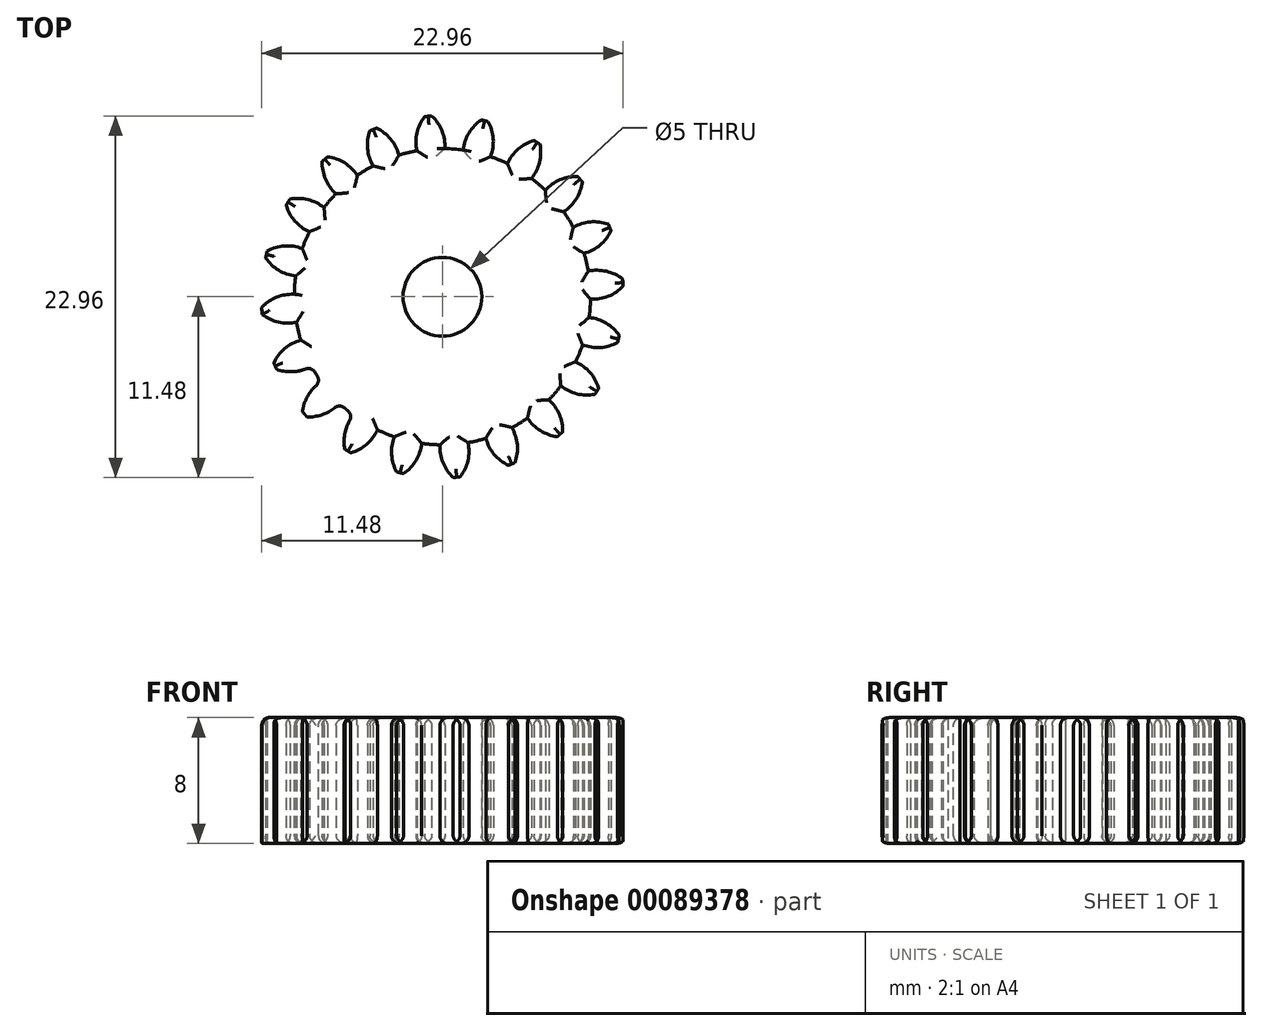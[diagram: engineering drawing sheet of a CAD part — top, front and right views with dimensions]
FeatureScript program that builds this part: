
annotation { "Feature Type Name" : "Feature", "Feature Type Description" : "" }
export const myFeature = defineFeature(function(context is Context, id is Id, definition is map)
    precondition{}
    {
        {
            assignVariable(context, id + "F0", {"name" : "GearDepth", "anyValue" : 8});
        }
        {
            assignVariable(context, id + "F1", {"name" : "TeethFillet", "anyValue" : 0.5});
        }
        {
            var Q0;
            Q0=qCreatedBy(makeId("Top.planeOp"),FACE);
            var sketch = newSketch(context, id + "F2", { "sketchPlane" : qUnion([Q0])});
            skCircle(sketch, "E0", {"center": v(0, 0) * mm, "radius": 9.4 * mm});
            skCircle(sketch, "E1", {"center": v(0, 0) * mm, "radius": 10.45 * mm, "construction": true});
            skCircle(sketch, "E2", {"center": v(0, 0) * mm, "radius": 11.5 * mm, "construction": true});
            skLineSegment(sketch, "E3", {"start": v(0, 0) * mm, "end": v(0, 17.6) * mm, "construction": true});
            skLineSegment(sketch, "E4", {"start": v(0, 0) * mm, "end": v(-1.42, 18) * mm, "construction": true});
            skLineSegment(sketch, "E5", {"start": v(0, 10.45) * mm, "end": v(-10.54, 10.45) * mm, "construction": true});
            skLineSegment(sketch, "E6", {"start": v(0, 10.45) * mm, "end": v(-10.3, 6.7) * mm, "construction": true});
            skCircle(sketch, "E7", {"center": v(0, 10.45) * mm, "radius": 2.61 * mm, "construction": true});
            skCircle(sketch, "E8", {"center": v(-2.46, 9.56) * mm, "radius": 2.61 * mm, "construction": true});
            skArc(sketch, "E9", {"start": v(-4.91, 10.45) * mm, "mid": v(-4.92, 10.42) * mm, "end": v(-4.94, 10.39) * mm});
            skArc(sketch, "E10.trimOffspring", {"start": v(0.15, 9.4) * mm, "mid": v(-0.03, 10.54) * mm, "end": v(-0.68, 11.48) * mm});
            skArc(sketch, "E11.MirrorCS", {"start": v(-1.62, 9.27) * mm, "mid": v(-1.62, 10.41) * mm, "end": v(-1.12, 11.45) * mm});
            skLineSegment(sketch, "E12", {"start": v(-1.12, 11.45) * mm, "end": v(-0.68, 11.48) * mm});
            skArc(sketch, "E13.1.0", {"start": v(-2.76, 9) * mm, "mid": v(-3.29, 10.01) * mm, "end": v(-4.2, 10.7) * mm});
            skLineSegment(sketch, "E13.1.1", {"start": v(-4.6, 10.54) * mm, "end": v(-4.2, 10.7) * mm});
            skArc(sketch, "E13.1.2", {"start": v(-4.4, 8.31) * mm, "mid": v(-4.76, 9.4) * mm, "end": v(-4.6, 10.54) * mm});
            skArc(sketch, "E13.2.0", {"start": v(-5.4, 7.7) * mm, "mid": v(-6.22, 8.5) * mm, "end": v(-7.3, 8.89) * mm});
            skLineSegment(sketch, "E13.2.1", {"start": v(-7.64, 8.6) * mm, "end": v(-7.3, 8.89) * mm});
            skArc(sketch, "E13.2.2", {"start": v(-6.76, 6.54) * mm, "mid": v(-7.43, 7.47) * mm, "end": v(-7.64, 8.6) * mm});
            skArc(sketch, "E13.3.0", {"start": v(-7.52, 5.65) * mm, "mid": v(-8.54, 6.17) * mm, "end": v(-9.69, 6.2) * mm});
            skLineSegment(sketch, "E13.3.1", {"start": v(-9.92, 5.82) * mm, "end": v(-9.69, 6.2) * mm});
            skArc(sketch, "E13.3.2", {"start": v(-8.45, 4.13) * mm, "mid": v(-9.37, 4.81) * mm, "end": v(-9.92, 5.82) * mm});
            skArc(sketch, "E13.4.0", {"start": v(-8.9, 3.05) * mm, "mid": v(-10.03, 3.23) * mm, "end": v(-11.13, 2.9) * mm});
            skLineSegment(sketch, "E13.4.1", {"start": v(-11.23, 2.47) * mm, "end": v(-11.13, 2.9) * mm});
            skArc(sketch, "E13.4.2", {"start": v(-9.32, 1.32) * mm, "mid": v(-10.4, 1.68) * mm, "end": v(-11.23, 2.47) * mm});
            skArc(sketch, "E13.5.0", {"start": v(-9.4, 0.15) * mm, "mid": v(-10.54, -0.03) * mm, "end": v(-11.48, -0.68) * mm});
            skLineSegment(sketch, "E13.5.1", {"start": v(-11.45, -1.12) * mm, "end": v(-11.48, -0.68) * mm});
            skArc(sketch, "E13.5.2", {"start": v(-9.27, -1.62) * mm, "mid": v(-10.41, -1.62) * mm, "end": v(-11.45, -1.12) * mm});
            skArc(sketch, "E13.6.0", {"start": v(-9, -2.76) * mm, "mid": v(-10.01, -3.29) * mm, "end": v(-10.7, -4.2) * mm});
            skLineSegment(sketch, "E13.6.1", {"start": v(-10.54, -4.6) * mm, "end": v(-10.7, -4.2) * mm});
            skArc(sketch, "E13.6.2", {"start": v(-8.31, -4.4) * mm, "mid": v(-9.4, -4.76) * mm, "end": v(-10.54, -4.6) * mm});
            skArc(sketch, "E13.7.0", {"start": v(-7.7, -5.4) * mm, "mid": v(-8.5, -6.22) * mm, "end": v(-8.89, -7.3) * mm});
            skLineSegment(sketch, "E13.7.1", {"start": v(-8.6, -7.64) * mm, "end": v(-8.89, -7.3) * mm});
            skArc(sketch, "E13.7.2", {"start": v(-6.54, -6.76) * mm, "mid": v(-7.47, -7.43) * mm, "end": v(-8.6, -7.64) * mm});
            skArc(sketch, "E13.8.0", {"start": v(-5.65, -7.52) * mm, "mid": v(-6.17, -8.54) * mm, "end": v(-6.2, -9.69) * mm});
            skLineSegment(sketch, "E13.8.1", {"start": v(-5.82, -9.92) * mm, "end": v(-6.2, -9.69) * mm});
            skArc(sketch, "E13.8.2", {"start": v(-4.13, -8.45) * mm, "mid": v(-4.81, -9.37) * mm, "end": v(-5.82, -9.92) * mm});
            skArc(sketch, "E13.9.0", {"start": v(-3.05, -8.9) * mm, "mid": v(-3.23, -10.03) * mm, "end": v(-2.9, -11.13) * mm});
            skLineSegment(sketch, "E13.9.1", {"start": v(-2.47, -11.23) * mm, "end": v(-2.9, -11.13) * mm});
            skArc(sketch, "E13.9.2", {"start": v(-1.32, -9.32) * mm, "mid": v(-1.68, -10.4) * mm, "end": v(-2.47, -11.23) * mm});
            skArc(sketch, "E13.10.0", {"start": v(-0.15, -9.4) * mm, "mid": v(0.03, -10.54) * mm, "end": v(0.68, -11.48) * mm});
            skLineSegment(sketch, "E13.10.1", {"start": v(1.12, -11.45) * mm, "end": v(0.68, -11.48) * mm});
            skArc(sketch, "E13.10.2", {"start": v(1.62, -9.27) * mm, "mid": v(1.62, -10.41) * mm, "end": v(1.12, -11.45) * mm});
            skArc(sketch, "E13.11.0", {"start": v(2.76, -9) * mm, "mid": v(3.29, -10.01) * mm, "end": v(4.2, -10.7) * mm});
            skLineSegment(sketch, "E13.11.1", {"start": v(4.6, -10.54) * mm, "end": v(4.2, -10.7) * mm});
            skArc(sketch, "E13.11.2", {"start": v(4.4, -8.31) * mm, "mid": v(4.76, -9.4) * mm, "end": v(4.6, -10.54) * mm});
            skArc(sketch, "E13.12.0", {"start": v(5.4, -7.7) * mm, "mid": v(6.22, -8.5) * mm, "end": v(7.3, -8.89) * mm});
            skLineSegment(sketch, "E13.12.1", {"start": v(7.64, -8.6) * mm, "end": v(7.3, -8.89) * mm});
            skArc(sketch, "E13.12.2", {"start": v(6.76, -6.54) * mm, "mid": v(7.43, -7.47) * mm, "end": v(7.64, -8.6) * mm});
            skArc(sketch, "E13.13.0", {"start": v(7.52, -5.65) * mm, "mid": v(8.54, -6.17) * mm, "end": v(9.69, -6.2) * mm});
            skLineSegment(sketch, "E13.13.1", {"start": v(9.92, -5.82) * mm, "end": v(9.69, -6.2) * mm});
            skArc(sketch, "E13.13.2", {"start": v(8.45, -4.13) * mm, "mid": v(9.37, -4.81) * mm, "end": v(9.92, -5.82) * mm});
            skArc(sketch, "E13.14.0", {"start": v(8.9, -3.05) * mm, "mid": v(10.03, -3.23) * mm, "end": v(11.13, -2.9) * mm});
            skLineSegment(sketch, "E13.14.1", {"start": v(11.23, -2.47) * mm, "end": v(11.13, -2.9) * mm});
            skArc(sketch, "E13.14.2", {"start": v(9.32, -1.32) * mm, "mid": v(10.4, -1.68) * mm, "end": v(11.23, -2.47) * mm});
            skArc(sketch, "E13.15.0", {"start": v(9.4, -0.15) * mm, "mid": v(10.54, 0.03) * mm, "end": v(11.48, 0.68) * mm});
            skLineSegment(sketch, "E13.15.1", {"start": v(11.45, 1.12) * mm, "end": v(11.48, 0.68) * mm});
            skArc(sketch, "E13.15.2", {"start": v(9.27, 1.62) * mm, "mid": v(10.41, 1.62) * mm, "end": v(11.45, 1.12) * mm});
            skArc(sketch, "E13.16.0", {"start": v(9, 2.76) * mm, "mid": v(10.01, 3.29) * mm, "end": v(10.7, 4.2) * mm});
            skLineSegment(sketch, "E13.16.1", {"start": v(10.54, 4.6) * mm, "end": v(10.7, 4.2) * mm});
            skArc(sketch, "E13.16.2", {"start": v(8.31, 4.4) * mm, "mid": v(9.4, 4.76) * mm, "end": v(10.54, 4.6) * mm});
            skArc(sketch, "E13.17.0", {"start": v(7.7, 5.4) * mm, "mid": v(8.5, 6.22) * mm, "end": v(8.89, 7.3) * mm});
            skLineSegment(sketch, "E13.17.1", {"start": v(8.6, 7.64) * mm, "end": v(8.89, 7.3) * mm});
            skArc(sketch, "E13.17.2", {"start": v(6.54, 6.76) * mm, "mid": v(7.47, 7.43) * mm, "end": v(8.6, 7.64) * mm});
            skArc(sketch, "E13.18.0", {"start": v(5.65, 7.52) * mm, "mid": v(6.17, 8.54) * mm, "end": v(6.2, 9.69) * mm});
            skLineSegment(sketch, "E13.18.1", {"start": v(5.82, 9.92) * mm, "end": v(6.2, 9.69) * mm});
            skArc(sketch, "E13.18.2", {"start": v(4.13, 8.45) * mm, "mid": v(4.81, 9.37) * mm, "end": v(5.82, 9.92) * mm});
            skArc(sketch, "E13.19.0", {"start": v(3.05, 8.9) * mm, "mid": v(3.23, 10.03) * mm, "end": v(2.9, 11.13) * mm});
            skLineSegment(sketch, "E13.19.1", {"start": v(2.47, 11.23) * mm, "end": v(2.9, 11.13) * mm});
            skArc(sketch, "E13.19.2", {"start": v(1.32, 9.32) * mm, "mid": v(1.68, 10.4) * mm, "end": v(2.47, 11.23) * mm});
            skCircle(sketch, "E14", {"center": v(0, 0) * mm, "radius": 2.5 * mm});
            skSolve(sketch);
        }
        {
            var Q0;
            {var subQ0=sQuery(id+"F2.wireOp",EDGE,"E10.trimOffspring");Q0=makeQuery(id+"F2.imprint","IMPRINT",FACE,{"disambiguationData":[TD([[makeQuery(id+"F2.imprint","IMPRINT",EDGE,{"derivedFrom":subQ0}),1.0]])]});}
            var Q1;
            {var subQ0=sQuery(id+"F2.wireOp",EDGE,"E0");var subQ1=makeQuery(id+"F2.imprint","INTERSECT",VERTEX,{"derivedFrom":[subQ0,sQuery(id+"F2.wireOp",EDGE,"E10.trimOffspring")]});Q1=makeQuery(id+"F2.imprint","IMPRINT",FACE,{"disambiguationData":[TD([[makeQuery(id+"F2.imprint","IMPRINT",EDGE,{"disambiguationData":[TD([[subQ1,-1.0]])],"derivedFrom":subQ0}),1.0]])]});}
            var Q2;
            {var subQ0=sQuery(id+"F2.wireOp",EDGE,"E13.1.0");Q2=makeQuery(id+"F2.imprint","IMPRINT",FACE,{"disambiguationData":[TD([[makeQuery(id+"F2.imprint","IMPRINT",EDGE,{"derivedFrom":subQ0}),1.0]])]});}
            var Q3;
            {var subQ0=sQuery(id+"F2.wireOp",EDGE,"E13.2.0");Q3=makeQuery(id+"F2.imprint","IMPRINT",FACE,{"disambiguationData":[TD([[makeQuery(id+"F2.imprint","IMPRINT",EDGE,{"derivedFrom":subQ0}),1.0]])]});}
            var Q4;
            {var subQ0=sQuery(id+"F2.wireOp",EDGE,"E13.3.0");Q4=makeQuery(id+"F2.imprint","IMPRINT",FACE,{"disambiguationData":[TD([[makeQuery(id+"F2.imprint","IMPRINT",EDGE,{"derivedFrom":subQ0}),1.0]])]});}
            var Q5;
            {var subQ0=sQuery(id+"F2.wireOp",EDGE,"E13.4.0");Q5=makeQuery(id+"F2.imprint","IMPRINT",FACE,{"disambiguationData":[TD([[makeQuery(id+"F2.imprint","IMPRINT",EDGE,{"derivedFrom":subQ0}),1.0]])]});}
            var Q6;
            {var subQ0=sQuery(id+"F2.wireOp",EDGE,"E13.5.0");Q6=makeQuery(id+"F2.imprint","IMPRINT",FACE,{"disambiguationData":[TD([[makeQuery(id+"F2.imprint","IMPRINT",EDGE,{"derivedFrom":subQ0}),1.0]])]});}
            var Q7;
            {var subQ0=sQuery(id+"F2.wireOp",EDGE,"E13.6.0");Q7=makeQuery(id+"F2.imprint","IMPRINT",FACE,{"disambiguationData":[TD([[makeQuery(id+"F2.imprint","IMPRINT",EDGE,{"derivedFrom":subQ0}),1.0]])]});}
            var Q8;
            {var subQ0=sQuery(id+"F2.wireOp",EDGE,"E13.7.0");Q8=makeQuery(id+"F2.imprint","IMPRINT",FACE,{"disambiguationData":[TD([[makeQuery(id+"F2.imprint","IMPRINT",EDGE,{"derivedFrom":subQ0}),1.0]])]});}
            var Q9;
            {var subQ0=sQuery(id+"F2.wireOp",EDGE,"E13.8.0");Q9=makeQuery(id+"F2.imprint","IMPRINT",FACE,{"disambiguationData":[TD([[makeQuery(id+"F2.imprint","IMPRINT",EDGE,{"derivedFrom":subQ0}),1.0]])]});}
            var Q10;
            {var subQ0=sQuery(id+"F2.wireOp",EDGE,"E13.9.0");Q10=makeQuery(id+"F2.imprint","IMPRINT",FACE,{"disambiguationData":[TD([[makeQuery(id+"F2.imprint","IMPRINT",EDGE,{"derivedFrom":subQ0}),1.0]])]});}
            var Q11;
            {var subQ0=sQuery(id+"F2.wireOp",EDGE,"E13.10.0");Q11=makeQuery(id+"F2.imprint","IMPRINT",FACE,{"disambiguationData":[TD([[makeQuery(id+"F2.imprint","IMPRINT",EDGE,{"derivedFrom":subQ0}),1.0]])]});}
            var Q12;
            {var subQ0=sQuery(id+"F2.wireOp",EDGE,"E13.11.0");Q12=makeQuery(id+"F2.imprint","IMPRINT",FACE,{"disambiguationData":[TD([[makeQuery(id+"F2.imprint","IMPRINT",EDGE,{"derivedFrom":subQ0}),1.0]])]});}
            var Q13;
            {var subQ0=sQuery(id+"F2.wireOp",EDGE,"E13.12.0");Q13=makeQuery(id+"F2.imprint","IMPRINT",FACE,{"disambiguationData":[TD([[makeQuery(id+"F2.imprint","IMPRINT",EDGE,{"derivedFrom":subQ0}),1.0]])]});}
            var Q14;
            {var subQ0=sQuery(id+"F2.wireOp",EDGE,"E13.13.0");Q14=makeQuery(id+"F2.imprint","IMPRINT",FACE,{"disambiguationData":[TD([[makeQuery(id+"F2.imprint","IMPRINT",EDGE,{"derivedFrom":subQ0}),1.0]])]});}
            var Q15;
            {var subQ0=sQuery(id+"F2.wireOp",EDGE,"E13.14.0");Q15=makeQuery(id+"F2.imprint","IMPRINT",FACE,{"disambiguationData":[TD([[makeQuery(id+"F2.imprint","IMPRINT",EDGE,{"derivedFrom":subQ0}),1.0]])]});}
            var Q16;
            {var subQ0=sQuery(id+"F2.wireOp",EDGE,"E13.15.0");Q16=makeQuery(id+"F2.imprint","IMPRINT",FACE,{"disambiguationData":[TD([[makeQuery(id+"F2.imprint","IMPRINT",EDGE,{"derivedFrom":subQ0}),1.0]])]});}
            var Q17;
            {var subQ0=sQuery(id+"F2.wireOp",EDGE,"E13.16.0");Q17=makeQuery(id+"F2.imprint","IMPRINT",FACE,{"disambiguationData":[TD([[makeQuery(id+"F2.imprint","IMPRINT",EDGE,{"derivedFrom":subQ0}),1.0]])]});}
            var Q18;
            {var subQ0=sQuery(id+"F2.wireOp",EDGE,"E13.17.0");Q18=makeQuery(id+"F2.imprint","IMPRINT",FACE,{"disambiguationData":[TD([[makeQuery(id+"F2.imprint","IMPRINT",EDGE,{"derivedFrom":subQ0}),1.0]])]});}
            var Q19;
            {var subQ0=sQuery(id+"F2.wireOp",EDGE,"E13.18.0");Q19=makeQuery(id+"F2.imprint","IMPRINT",FACE,{"disambiguationData":[TD([[makeQuery(id+"F2.imprint","IMPRINT",EDGE,{"derivedFrom":subQ0}),1.0]])]});}
            var Q20;
            {var subQ0=sQuery(id+"F2.wireOp",EDGE,"E13.19.0");Q20=makeQuery(id+"F2.imprint","IMPRINT",FACE,{"disambiguationData":[TD([[makeQuery(id+"F2.imprint","IMPRINT",EDGE,{"derivedFrom":subQ0}),1.0]])]});}
            var Q21;
            Q21=sQuery(id+"F2.wireOp",EDGE,"E0");
            var Q22;
            Q22=sQuery(id+"F2.wireOp",EDGE,"E10.trimOffspring");
            var Q23;
            Q23=sQuery(id+"F2.wireOp",EDGE,"E12");
            var Q24;
            Q24=sQuery(id+"F2.wireOp",EDGE,"E11.MirrorCS");
            extrude(context, id + "F3", {"entities" : qUnion([Q0, Q1, Q2, Q3, Q4, Q5, Q6, Q7, Q8, Q9, Q10, Q11, Q12, Q13, Q14, Q15, Q16, Q17, Q18, Q19, Q20]), "surfaceEntities" : qUnion([Q21, Q22, Q23, Q24]), "depth" : (getVariable(context, 'GearDepth')) * mm});
        }
        {
            var Q0;
            Q0=makeQuery(id+"F3.opExtrude","CAP_EDGE",EDGE,{"disambiguationData":[OSD([sQuery(id+"F2.wireOp",EDGE,"E13.5.2")])],"isStart":false});
            var Q1;
            Q1=makeQuery(id+"F3.opExtrude","CAP_EDGE",EDGE,{"disambiguationData":[OSD([sQuery(id+"F2.wireOp",EDGE,"E13.5.1")])],"isStart":false});
            var Q2;
            {var subQ0=sQuery(id+"F2.wireOp",EDGE,"E0");Q2=makeQuery(id+"F3.opExtrude","CAP_EDGE",EDGE,{"disambiguationData":[OSD([subQ0]),TDD([makeQuery(id+"F2.imprint","IMPRINT",EDGE,{"disambiguationData":[TD([[makeQuery(id+"F2.imprint","INTERSECT",VERTEX,{"derivedFrom":[subQ0,sQuery(id+"F2.wireOp",EDGE,"E13.5.2")]}),-1.0]])],"derivedFrom":subQ0})])],"isStart":false});}
            var Q3;
            Q3=makeQuery(id+"F3.opExtrude","CAP_EDGE",EDGE,{"disambiguationData":[OSD([sQuery(id+"F2.wireOp",EDGE,"E13.6.0")])],"isStart":false});
            var Q4;
            Q4=makeQuery(id+"F3.opExtrude","CAP_EDGE",EDGE,{"disambiguationData":[OSD([sQuery(id+"F2.wireOp",EDGE,"E13.6.1")])],"isStart":false});
            var Q5;
            Q5=makeQuery(id+"F3.opExtrude","CAP_EDGE",EDGE,{"disambiguationData":[OSD([sQuery(id+"F2.wireOp",EDGE,"E13.6.2")])],"isStart":false});
            var Q6;
            {var subQ0=sQuery(id+"F2.wireOp",EDGE,"E0");Q6=makeQuery(id+"F3.opExtrude","SWEPT_FACE",FACE,{"disambiguationData":[OSD([subQ0]),TDD([makeQuery(id+"F2.imprint","IMPRINT",EDGE,{"disambiguationData":[TD([[makeQuery(id+"F2.imprint","INTERSECT",VERTEX,{"derivedFrom":[subQ0,sQuery(id+"F2.wireOp",EDGE,"E13.6.2")]}),-1.0]])],"derivedFrom":subQ0})])]});}
            var Q7;
            {var subQ0=sQuery(id+"F2.wireOp",EDGE,"E0");Q7=makeQuery(id+"F3.opExtrude","CAP_EDGE",EDGE,{"disambiguationData":[OSD([subQ0]),TDD([makeQuery(id+"F2.imprint","IMPRINT",EDGE,{"disambiguationData":[TD([[makeQuery(id+"F2.imprint","INTERSECT",VERTEX,{"derivedFrom":[subQ0,sQuery(id+"F2.wireOp",EDGE,"E13.6.2")]}),-1.0]])],"derivedFrom":subQ0})])],"isStart":false});}
            var Q8;
            Q8=makeQuery(id+"F3.opExtrude","CAP_EDGE",EDGE,{"disambiguationData":[OSD([sQuery(id+"F2.wireOp",EDGE,"E13.7.2")])],"isStart":true});
            var Q9;
            {var subQ0=sQuery(id+"F2.wireOp",EDGE,"E0");Q9=makeQuery(id+"F3.opExtrude","CAP_EDGE",EDGE,{"disambiguationData":[OSD([subQ0]),TDD([makeQuery(id+"F2.imprint","IMPRINT",EDGE,{"disambiguationData":[TD([[makeQuery(id+"F2.imprint","INTERSECT",VERTEX,{"derivedFrom":[subQ0,sQuery(id+"F2.wireOp",EDGE,"E13.7.2")]}),-1.0]])],"derivedFrom":subQ0})])],"isStart":true});}
            var Q10;
            Q10=makeQuery(id+"F3.opExtrude","CAP_EDGE",EDGE,{"disambiguationData":[OSD([sQuery(id+"F2.wireOp",EDGE,"E13.7.2")])],"isStart":false});
            var Q11;
            {var subQ0=sQuery(id+"F2.wireOp",EDGE,"E0");Q11=makeQuery(id+"F3.opExtrude","CAP_EDGE",EDGE,{"disambiguationData":[OSD([subQ0]),TDD([makeQuery(id+"F2.imprint","IMPRINT",EDGE,{"disambiguationData":[TD([[makeQuery(id+"F2.imprint","INTERSECT",VERTEX,{"derivedFrom":[subQ0,sQuery(id+"F2.wireOp",EDGE,"E13.7.2")]}),-1.0]])],"derivedFrom":subQ0})])],"isStart":false});}
            var Q12;
            Q12=makeQuery(id+"F3.opExtrude","CAP_EDGE",EDGE,{"disambiguationData":[OSD([sQuery(id+"F2.wireOp",EDGE,"E13.8.0")])],"isStart":false});
            var Q13;
            {var subQ0=sQuery(id+"F2.wireOp",EDGE,"E0");Q13=makeQuery(id+"F3.opExtrude","SWEPT_FACE",FACE,{"disambiguationData":[OSD([subQ0]),TDD([makeQuery(id+"F2.imprint","IMPRINT",EDGE,{"disambiguationData":[TD([[makeQuery(id+"F2.imprint","INTERSECT",VERTEX,{"derivedFrom":[subQ0,sQuery(id+"F2.wireOp",EDGE,"E13.7.2")]}),-1.0]])],"derivedFrom":subQ0})])]});}
            var Q14;
            Q14=makeQuery(id+"F3.opExtrude","CAP_EDGE",EDGE,{"disambiguationData":[OSD([sQuery(id+"F2.wireOp",EDGE,"E13.6.0")])],"isStart":true});
            var Q15;
            Q15=makeQuery(id+"F3.opExtrude","CAP_EDGE",EDGE,{"disambiguationData":[OSD([sQuery(id+"F2.wireOp",EDGE,"E13.8.2")])],"isStart":false});
            var Q16;
            {var subQ0=sQuery(id+"F2.wireOp",EDGE,"E0");Q16=makeQuery(id+"F3.opExtrude","CAP_EDGE",EDGE,{"disambiguationData":[OSD([subQ0]),TDD([makeQuery(id+"F2.imprint","IMPRINT",EDGE,{"disambiguationData":[TD([[makeQuery(id+"F2.imprint","INTERSECT",VERTEX,{"derivedFrom":[subQ0,sQuery(id+"F2.wireOp",EDGE,"E13.8.2")]}),-1.0]])],"derivedFrom":subQ0})])],"isStart":false});}
            var Q17;
            Q17=makeQuery(id+"F3.opExtrude","CAP_EDGE",EDGE,{"disambiguationData":[OSD([sQuery(id+"F2.wireOp",EDGE,"E13.9.0")])],"isStart":false});
            var Q18;
            Q18=makeQuery(id+"F3.opExtrude","CAP_EDGE",EDGE,{"disambiguationData":[OSD([sQuery(id+"F2.wireOp",EDGE,"E13.9.2")])],"isStart":false});
            var Q19;
            {var subQ0=sQuery(id+"F2.wireOp",EDGE,"E0");Q19=makeQuery(id+"F3.opExtrude","CAP_EDGE",EDGE,{"disambiguationData":[OSD([subQ0]),TDD([makeQuery(id+"F2.imprint","IMPRINT",EDGE,{"disambiguationData":[TD([[makeQuery(id+"F2.imprint","INTERSECT",VERTEX,{"derivedFrom":[subQ0,sQuery(id+"F2.wireOp",EDGE,"E13.9.2")]}),-1.0]])],"derivedFrom":subQ0})])],"isStart":false});}
            var Q20;
            Q20=makeQuery(id+"F3.opExtrude","CAP_EDGE",EDGE,{"disambiguationData":[OSD([sQuery(id+"F2.wireOp",EDGE,"E13.10.0")])],"isStart":false});
            var Q21;
            Q21=makeQuery(id+"F3.opExtrude","CAP_EDGE",EDGE,{"disambiguationData":[OSD([sQuery(id+"F2.wireOp",EDGE,"E13.10.2")])],"isStart":false});
            var Q22;
            {var subQ0=sQuery(id+"F2.wireOp",EDGE,"E0");Q22=makeQuery(id+"F3.opExtrude","CAP_EDGE",EDGE,{"disambiguationData":[OSD([subQ0]),TDD([makeQuery(id+"F2.imprint","IMPRINT",EDGE,{"disambiguationData":[TD([[makeQuery(id+"F2.imprint","INTERSECT",VERTEX,{"derivedFrom":[subQ0,sQuery(id+"F2.wireOp",EDGE,"E13.10.2")]}),-1.0]])],"derivedFrom":subQ0})])],"isStart":false});}
            var Q23;
            Q23=makeQuery(id+"F3.opExtrude","CAP_EDGE",EDGE,{"disambiguationData":[OSD([sQuery(id+"F2.wireOp",EDGE,"E13.11.0")])],"isStart":false});
            var Q24;
            Q24=makeQuery(id+"F3.opExtrude","CAP_EDGE",EDGE,{"disambiguationData":[OSD([sQuery(id+"F2.wireOp",EDGE,"E13.11.2")])],"isStart":false});
            var Q25;
            {var subQ0=sQuery(id+"F2.wireOp",EDGE,"E0");Q25=makeQuery(id+"F3.opExtrude","CAP_EDGE",EDGE,{"disambiguationData":[OSD([subQ0]),TDD([makeQuery(id+"F2.imprint","IMPRINT",EDGE,{"disambiguationData":[TD([[makeQuery(id+"F2.imprint","INTERSECT",VERTEX,{"derivedFrom":[subQ0,sQuery(id+"F2.wireOp",EDGE,"E13.11.2")]}),-1.0]])],"derivedFrom":subQ0})])],"isStart":false});}
            var Q26;
            Q26=makeQuery(id+"F3.opExtrude","CAP_EDGE",EDGE,{"disambiguationData":[OSD([sQuery(id+"F2.wireOp",EDGE,"E13.12.0")])],"isStart":false});
            var Q27;
            Q27=makeQuery(id+"F3.opExtrude","CAP_EDGE",EDGE,{"disambiguationData":[OSD([sQuery(id+"F2.wireOp",EDGE,"E13.12.2")])],"isStart":false});
            var Q28;
            {var subQ0=sQuery(id+"F2.wireOp",EDGE,"E0");Q28=makeQuery(id+"F3.opExtrude","CAP_EDGE",EDGE,{"disambiguationData":[OSD([subQ0]),TDD([makeQuery(id+"F2.imprint","IMPRINT",EDGE,{"disambiguationData":[TD([[makeQuery(id+"F2.imprint","INTERSECT",VERTEX,{"derivedFrom":[subQ0,sQuery(id+"F2.wireOp",EDGE,"E13.12.2")]}),-1.0]])],"derivedFrom":subQ0})])],"isStart":false});}
            var Q29;
            Q29=makeQuery(id+"F3.opExtrude","CAP_EDGE",EDGE,{"disambiguationData":[OSD([sQuery(id+"F2.wireOp",EDGE,"E13.13.0")])],"isStart":false});
            var Q30;
            Q30=makeQuery(id+"F3.opExtrude","CAP_EDGE",EDGE,{"disambiguationData":[OSD([sQuery(id+"F2.wireOp",EDGE,"E13.13.2")])],"isStart":false});
            var Q31;
            {var subQ0=sQuery(id+"F2.wireOp",EDGE,"E0");Q31=makeQuery(id+"F3.opExtrude","CAP_EDGE",EDGE,{"disambiguationData":[OSD([subQ0]),TDD([makeQuery(id+"F2.imprint","IMPRINT",EDGE,{"disambiguationData":[TD([[makeQuery(id+"F2.imprint","INTERSECT",VERTEX,{"derivedFrom":[subQ0,sQuery(id+"F2.wireOp",EDGE,"E13.13.2")]}),-1.0]])],"derivedFrom":subQ0})])],"isStart":false});}
            var Q32;
            Q32=makeQuery(id+"F3.opExtrude","CAP_EDGE",EDGE,{"disambiguationData":[OSD([sQuery(id+"F2.wireOp",EDGE,"E13.14.0")])],"isStart":false});
            var Q33;
            Q33=makeQuery(id+"F3.opExtrude","CAP_EDGE",EDGE,{"disambiguationData":[OSD([sQuery(id+"F2.wireOp",EDGE,"E13.14.2")])],"isStart":false});
            var Q34;
            {var subQ0=sQuery(id+"F2.wireOp",EDGE,"E0");Q34=makeQuery(id+"F3.opExtrude","CAP_EDGE",EDGE,{"disambiguationData":[OSD([subQ0]),TDD([makeQuery(id+"F2.imprint","IMPRINT",EDGE,{"disambiguationData":[TD([[makeQuery(id+"F2.imprint","INTERSECT",VERTEX,{"derivedFrom":[subQ0,sQuery(id+"F2.wireOp",EDGE,"E13.14.2")]}),-1.0]])],"derivedFrom":subQ0})])],"isStart":false});}
            var Q35;
            Q35=makeQuery(id+"F3.opExtrude","CAP_EDGE",EDGE,{"disambiguationData":[OSD([sQuery(id+"F2.wireOp",EDGE,"E13.15.0")])],"isStart":false});
            var Q36;
            {var subQ0=sQuery(id+"F2.wireOp",EDGE,"E0");Q36=makeQuery(id+"F3.opExtrude","CAP_EDGE",EDGE,{"disambiguationData":[OSD([subQ0]),TDD([makeQuery(id+"F2.imprint","IMPRINT",EDGE,{"disambiguationData":[TD([[makeQuery(id+"F2.imprint","INTERSECT",VERTEX,{"derivedFrom":[subQ0,sQuery(id+"F2.wireOp",EDGE,"E13.14.2")]}),-1.0]])],"derivedFrom":subQ0})])],"isStart":false});}
            var Q37;
            Q37=makeQuery(id+"F3.opExtrude","CAP_EDGE",EDGE,{"disambiguationData":[OSD([sQuery(id+"F2.wireOp",EDGE,"E13.15.2")])],"isStart":false});
            var Q38;
            {var subQ0=sQuery(id+"F2.wireOp",EDGE,"E0");Q38=makeQuery(id+"F3.opExtrude","CAP_EDGE",EDGE,{"disambiguationData":[OSD([subQ0]),TDD([makeQuery(id+"F2.imprint","IMPRINT",EDGE,{"disambiguationData":[TD([[makeQuery(id+"F2.imprint","INTERSECT",VERTEX,{"derivedFrom":[subQ0,sQuery(id+"F2.wireOp",EDGE,"E13.15.2")]}),-1.0]])],"derivedFrom":subQ0})])],"isStart":false});}
            var Q39;
            Q39=makeQuery(id+"F3.opExtrude","CAP_EDGE",EDGE,{"disambiguationData":[OSD([sQuery(id+"F2.wireOp",EDGE,"E13.16.0")])],"isStart":false});
            var Q40;
            Q40=makeQuery(id+"F3.opExtrude","CAP_EDGE",EDGE,{"disambiguationData":[OSD([sQuery(id+"F2.wireOp",EDGE,"E13.16.2")])],"isStart":false});
            var Q41;
            Q41=makeQuery(id+"F3.opExtrude","CAP_EDGE",EDGE,{"disambiguationData":[OSD([sQuery(id+"F2.wireOp",EDGE,"E13.17.0")])],"isStart":false});
            var Q42;
            {var subQ0=sQuery(id+"F2.wireOp",EDGE,"E0");Q42=makeQuery(id+"F3.opExtrude","CAP_EDGE",EDGE,{"disambiguationData":[OSD([subQ0]),TDD([makeQuery(id+"F2.imprint","IMPRINT",EDGE,{"disambiguationData":[TD([[makeQuery(id+"F2.imprint","INTERSECT",VERTEX,{"derivedFrom":[subQ0,sQuery(id+"F2.wireOp",EDGE,"E13.16.2")]}),-1.0]])],"derivedFrom":subQ0})])],"isStart":false});}
            var Q43;
            Q43=makeQuery(id+"F3.opExtrude","CAP_EDGE",EDGE,{"disambiguationData":[OSD([sQuery(id+"F2.wireOp",EDGE,"E13.17.2")])],"isStart":false});
            var Q44;
            {var subQ0=sQuery(id+"F2.wireOp",EDGE,"E0");Q44=makeQuery(id+"F3.opExtrude","CAP_EDGE",EDGE,{"disambiguationData":[OSD([subQ0]),TDD([makeQuery(id+"F2.imprint","IMPRINT",EDGE,{"disambiguationData":[TD([[makeQuery(id+"F2.imprint","INTERSECT",VERTEX,{"derivedFrom":[subQ0,sQuery(id+"F2.wireOp",EDGE,"E13.17.2")]}),-1.0]])],"derivedFrom":subQ0})])],"isStart":false});}
            var Q45;
            Q45=makeQuery(id+"F3.opExtrude","CAP_EDGE",EDGE,{"disambiguationData":[OSD([sQuery(id+"F2.wireOp",EDGE,"E13.18.0")])],"isStart":false});
            var Q46;
            Q46=makeQuery(id+"F3.opExtrude","CAP_EDGE",EDGE,{"disambiguationData":[OSD([sQuery(id+"F2.wireOp",EDGE,"E13.18.2")])],"isStart":false});
            var Q47;
            {var subQ0=sQuery(id+"F2.wireOp",EDGE,"E0");Q47=makeQuery(id+"F3.opExtrude","CAP_EDGE",EDGE,{"disambiguationData":[OSD([subQ0]),TDD([makeQuery(id+"F2.imprint","IMPRINT",EDGE,{"disambiguationData":[TD([[makeQuery(id+"F2.imprint","INTERSECT",VERTEX,{"derivedFrom":[subQ0,sQuery(id+"F2.wireOp",EDGE,"E13.18.2")]}),-1.0]])],"derivedFrom":subQ0})])],"isStart":false});}
            var Q48;
            Q48=makeQuery(id+"F3.opExtrude","CAP_EDGE",EDGE,{"disambiguationData":[OSD([sQuery(id+"F2.wireOp",EDGE,"E13.19.0")])],"isStart":false});
            var Q49;
            Q49=makeQuery(id+"F3.opExtrude","CAP_EDGE",EDGE,{"disambiguationData":[OSD([sQuery(id+"F2.wireOp",EDGE,"E13.19.2")])],"isStart":false});
            var Q50;
            Q50=makeQuery(id+"F3.opExtrude","CAP_EDGE",EDGE,{"disambiguationData":[OSD([sQuery(id+"F2.wireOp",EDGE,"E10.trimOffspring")])],"isStart":false});
            var Q51;
            Q51=makeQuery(id+"F3.opExtrude","CAP_EDGE",EDGE,{"disambiguationData":[OSD([sQuery(id+"F2.wireOp",EDGE,"E11.MirrorCS")])],"isStart":false});
            var Q52;
            {var subQ0=sQuery(id+"F2.wireOp",EDGE,"E0");Q52=makeQuery(id+"F3.opExtrude","CAP_EDGE",EDGE,{"disambiguationData":[OSD([subQ0]),TDD([makeQuery(id+"F2.imprint","IMPRINT",EDGE,{"disambiguationData":[TD([[makeQuery(id+"F2.imprint","INTERSECT",VERTEX,{"derivedFrom":[subQ0,sQuery(id+"F2.wireOp",EDGE,"E11.MirrorCS")]}),-1.0]])],"derivedFrom":subQ0})])],"isStart":false});}
            var Q53;
            Q53=makeQuery(id+"F3.opExtrude","CAP_EDGE",EDGE,{"disambiguationData":[OSD([sQuery(id+"F2.wireOp",EDGE,"E13.1.0")])],"isStart":false});
            var Q54;
            Q54=makeQuery(id+"F3.opExtrude","CAP_EDGE",EDGE,{"disambiguationData":[OSD([sQuery(id+"F2.wireOp",EDGE,"E13.1.2")])],"isStart":false});
            var Q55;
            {var subQ0=sQuery(id+"F2.wireOp",EDGE,"E0");Q55=makeQuery(id+"F3.opExtrude","CAP_EDGE",EDGE,{"disambiguationData":[OSD([subQ0]),TDD([makeQuery(id+"F2.imprint","IMPRINT",EDGE,{"disambiguationData":[TD([[makeQuery(id+"F2.imprint","INTERSECT",VERTEX,{"derivedFrom":[subQ0,sQuery(id+"F2.wireOp",EDGE,"E13.1.2")]}),-1.0]])],"derivedFrom":subQ0})])],"isStart":false});}
            var Q56;
            Q56=makeQuery(id+"F3.opExtrude","CAP_EDGE",EDGE,{"disambiguationData":[OSD([sQuery(id+"F2.wireOp",EDGE,"E13.2.0")])],"isStart":false});
            var Q57;
            Q57=makeQuery(id+"F3.opExtrude","CAP_EDGE",EDGE,{"disambiguationData":[OSD([sQuery(id+"F2.wireOp",EDGE,"E13.2.2")])],"isStart":false});
            var Q58;
            {var subQ0=sQuery(id+"F2.wireOp",EDGE,"E0");Q58=makeQuery(id+"F3.opExtrude","CAP_EDGE",EDGE,{"disambiguationData":[OSD([subQ0]),TDD([makeQuery(id+"F2.imprint","IMPRINT",EDGE,{"disambiguationData":[TD([[makeQuery(id+"F2.imprint","INTERSECT",VERTEX,{"derivedFrom":[subQ0,sQuery(id+"F2.wireOp",EDGE,"E13.2.2")]}),-1.0]])],"derivedFrom":subQ0})])],"isStart":false});}
            var Q59;
            Q59=makeQuery(id+"F3.opExtrude","CAP_EDGE",EDGE,{"disambiguationData":[OSD([sQuery(id+"F2.wireOp",EDGE,"E13.3.0")])],"isStart":false});
            var Q60;
            Q60=makeQuery(id+"F3.opExtrude","CAP_EDGE",EDGE,{"disambiguationData":[OSD([sQuery(id+"F2.wireOp",EDGE,"E13.3.2")])],"isStart":false});
            var Q61;
            {var subQ0=sQuery(id+"F2.wireOp",EDGE,"E0");Q61=makeQuery(id+"F3.opExtrude","CAP_EDGE",EDGE,{"disambiguationData":[OSD([subQ0]),TDD([makeQuery(id+"F2.imprint","IMPRINT",EDGE,{"disambiguationData":[TD([[makeQuery(id+"F2.imprint","INTERSECT",VERTEX,{"derivedFrom":[subQ0,sQuery(id+"F2.wireOp",EDGE,"E13.3.2")]}),-1.0]])],"derivedFrom":subQ0})])],"isStart":false});}
            var Q62;
            Q62=makeQuery(id+"F3.opExtrude","CAP_EDGE",EDGE,{"disambiguationData":[OSD([sQuery(id+"F2.wireOp",EDGE,"E13.4.0")])],"isStart":false});
            var Q63;
            Q63=makeQuery(id+"F3.opExtrude","CAP_EDGE",EDGE,{"disambiguationData":[OSD([sQuery(id+"F2.wireOp",EDGE,"E13.4.2")])],"isStart":false});
            var Q64;
            {var subQ0=sQuery(id+"F2.wireOp",EDGE,"E0");Q64=makeQuery(id+"F3.opExtrude","CAP_EDGE",EDGE,{"disambiguationData":[OSD([subQ0]),TDD([makeQuery(id+"F2.imprint","IMPRINT",EDGE,{"disambiguationData":[TD([[makeQuery(id+"F2.imprint","INTERSECT",VERTEX,{"derivedFrom":[subQ0,sQuery(id+"F2.wireOp",EDGE,"E13.4.2")]}),-1.0]])],"derivedFrom":subQ0})])],"isStart":false});}
            var Q65;
            {var subQ0=sQuery(id+"F2.wireOp",EDGE,"E0");Q65=makeQuery(id+"F3.opExtrude","CAP_EDGE",EDGE,{"disambiguationData":[OSD([subQ0]),TDD([makeQuery(id+"F2.imprint","IMPRINT",EDGE,{"disambiguationData":[TD([[makeQuery(id+"F2.imprint","INTERSECT",VERTEX,{"derivedFrom":[subQ0,sQuery(id+"F2.wireOp",EDGE,"E13.5.2")]}),-1.0]])],"derivedFrom":subQ0})])],"isStart":true});}
            var Q66;
            Q66=makeQuery(id+"F3.opExtrude","CAP_EDGE",EDGE,{"disambiguationData":[OSD([sQuery(id+"F2.wireOp",EDGE,"E13.5.2")])],"isStart":true});
            var Q67;
            {var subQ0=sQuery(id+"F2.wireOp",EDGE,"E0");Q67=makeQuery(id+"F3.opExtrude","CAP_EDGE",EDGE,{"disambiguationData":[OSD([subQ0]),TDD([makeQuery(id+"F2.imprint","IMPRINT",EDGE,{"disambiguationData":[TD([[makeQuery(id+"F2.imprint","INTERSECT",VERTEX,{"derivedFrom":[subQ0,sQuery(id+"F2.wireOp",EDGE,"E13.4.2")]}),-1.0]])],"derivedFrom":subQ0})])],"isStart":true});}
            var Q68;
            Q68=makeQuery(id+"F3.opExtrude","CAP_EDGE",EDGE,{"disambiguationData":[OSD([sQuery(id+"F2.wireOp",EDGE,"E13.4.2")])],"isStart":true});
            var Q69;
            Q69=makeQuery(id+"F3.opExtrude","CAP_EDGE",EDGE,{"disambiguationData":[OSD([sQuery(id+"F2.wireOp",EDGE,"E13.4.0")])],"isStart":true});
            var Q70;
            {var subQ0=sQuery(id+"F2.wireOp",EDGE,"E0");Q70=makeQuery(id+"F3.opExtrude","CAP_EDGE",EDGE,{"disambiguationData":[OSD([subQ0]),TDD([makeQuery(id+"F2.imprint","IMPRINT",EDGE,{"disambiguationData":[TD([[makeQuery(id+"F2.imprint","INTERSECT",VERTEX,{"derivedFrom":[subQ0,sQuery(id+"F2.wireOp",EDGE,"E13.3.2")]}),-1.0]])],"derivedFrom":subQ0})])],"isStart":true});}
            var Q71;
            Q71=makeQuery(id+"F3.opExtrude","CAP_EDGE",EDGE,{"disambiguationData":[OSD([sQuery(id+"F2.wireOp",EDGE,"E13.3.2")])],"isStart":true});
            var Q72;
            Q72=makeQuery(id+"F3.opExtrude","CAP_EDGE",EDGE,{"disambiguationData":[OSD([sQuery(id+"F2.wireOp",EDGE,"E13.3.0")])],"isStart":true});
            var Q73;
            {var subQ0=sQuery(id+"F2.wireOp",EDGE,"E0");Q73=makeQuery(id+"F3.opExtrude","CAP_EDGE",EDGE,{"disambiguationData":[OSD([subQ0]),TDD([makeQuery(id+"F2.imprint","IMPRINT",EDGE,{"disambiguationData":[TD([[makeQuery(id+"F2.imprint","INTERSECT",VERTEX,{"derivedFrom":[subQ0,sQuery(id+"F2.wireOp",EDGE,"E13.2.2")]}),-1.0]])],"derivedFrom":subQ0})])],"isStart":true});}
            var Q74;
            Q74=makeQuery(id+"F3.opExtrude","CAP_EDGE",EDGE,{"disambiguationData":[OSD([sQuery(id+"F2.wireOp",EDGE,"E13.2.2")])],"isStart":true});
            var Q75;
            Q75=makeQuery(id+"F3.opExtrude","CAP_EDGE",EDGE,{"disambiguationData":[OSD([sQuery(id+"F2.wireOp",EDGE,"E13.2.0")])],"isStart":true});
            var Q76;
            Q76=makeQuery(id+"F3.opExtrude","CAP_EDGE",EDGE,{"disambiguationData":[OSD([sQuery(id+"F2.wireOp",EDGE,"E13.1.2")])],"isStart":true});
            var Q77;
            {var subQ0=sQuery(id+"F2.wireOp",EDGE,"E0");Q77=makeQuery(id+"F3.opExtrude","CAP_EDGE",EDGE,{"disambiguationData":[OSD([subQ0]),TDD([makeQuery(id+"F2.imprint","IMPRINT",EDGE,{"disambiguationData":[TD([[makeQuery(id+"F2.imprint","INTERSECT",VERTEX,{"derivedFrom":[subQ0,sQuery(id+"F2.wireOp",EDGE,"E13.1.2")]}),-1.0]])],"derivedFrom":subQ0})])],"isStart":true});}
            var Q78;
            Q78=makeQuery(id+"F3.opExtrude","CAP_EDGE",EDGE,{"disambiguationData":[OSD([sQuery(id+"F2.wireOp",EDGE,"E13.1.0")])],"isStart":true});
            var Q79;
            {var subQ0=sQuery(id+"F2.wireOp",EDGE,"E0");Q79=makeQuery(id+"F3.opExtrude","CAP_EDGE",EDGE,{"disambiguationData":[OSD([subQ0]),TDD([makeQuery(id+"F2.imprint","IMPRINT",EDGE,{"disambiguationData":[TD([[makeQuery(id+"F2.imprint","INTERSECT",VERTEX,{"derivedFrom":[subQ0,sQuery(id+"F2.wireOp",EDGE,"E11.MirrorCS")]}),-1.0]])],"derivedFrom":subQ0})])],"isStart":true});}
            var Q80;
            Q80=makeQuery(id+"F3.opExtrude","CAP_EDGE",EDGE,{"disambiguationData":[OSD([sQuery(id+"F2.wireOp",EDGE,"E11.MirrorCS")])],"isStart":true});
            var Q81;
            Q81=makeQuery(id+"F3.opExtrude","CAP_EDGE",EDGE,{"disambiguationData":[OSD([sQuery(id+"F2.wireOp",EDGE,"E10.trimOffspring")])],"isStart":true});
            var Q82;
            {var subQ0=sQuery(id+"F2.wireOp",EDGE,"E0");Q82=makeQuery(id+"F3.opExtrude","CAP_EDGE",EDGE,{"disambiguationData":[OSD([subQ0]),TDD([makeQuery(id+"F2.imprint","IMPRINT",EDGE,{"disambiguationData":[TD([[makeQuery(id+"F2.imprint","INTERSECT",VERTEX,{"derivedFrom":[subQ0,sQuery(id+"F2.wireOp",EDGE,"E10.trimOffspring")]}),1.0]])],"derivedFrom":subQ0})])],"isStart":true});}
            var Q83;
            Q83=makeQuery(id+"F3.opExtrude","CAP_EDGE",EDGE,{"disambiguationData":[OSD([sQuery(id+"F2.wireOp",EDGE,"E13.19.2")])],"isStart":true});
            var Q84;
            Q84=makeQuery(id+"F3.opExtrude","CAP_EDGE",EDGE,{"disambiguationData":[OSD([sQuery(id+"F2.wireOp",EDGE,"E13.19.0")])],"isStart":true});
            var Q85;
            {var subQ0=sQuery(id+"F2.wireOp",EDGE,"E0");Q85=makeQuery(id+"F3.opExtrude","CAP_EDGE",EDGE,{"disambiguationData":[OSD([subQ0]),TDD([makeQuery(id+"F2.imprint","IMPRINT",EDGE,{"disambiguationData":[TD([[makeQuery(id+"F2.imprint","INTERSECT",VERTEX,{"derivedFrom":[subQ0,sQuery(id+"F2.wireOp",EDGE,"E13.18.2")]}),-1.0]])],"derivedFrom":subQ0})])],"isStart":true});}
            var Q86;
            Q86=makeQuery(id+"F3.opExtrude","CAP_EDGE",EDGE,{"disambiguationData":[OSD([sQuery(id+"F2.wireOp",EDGE,"E13.18.2")])],"isStart":true});
            var Q87;
            Q87=makeQuery(id+"F3.opExtrude","CAP_EDGE",EDGE,{"disambiguationData":[OSD([sQuery(id+"F2.wireOp",EDGE,"E13.18.0")])],"isStart":true});
            var Q88;
            {var subQ0=sQuery(id+"F2.wireOp",EDGE,"E0");Q88=makeQuery(id+"F3.opExtrude","CAP_EDGE",EDGE,{"disambiguationData":[OSD([subQ0]),TDD([makeQuery(id+"F2.imprint","IMPRINT",EDGE,{"disambiguationData":[TD([[makeQuery(id+"F2.imprint","INTERSECT",VERTEX,{"derivedFrom":[subQ0,sQuery(id+"F2.wireOp",EDGE,"E13.17.2")]}),-1.0]])],"derivedFrom":subQ0})])],"isStart":true});}
            var Q89;
            Q89=makeQuery(id+"F3.opExtrude","CAP_EDGE",EDGE,{"disambiguationData":[OSD([sQuery(id+"F2.wireOp",EDGE,"E13.17.2")])],"isStart":true});
            var Q90;
            Q90=makeQuery(id+"F3.opExtrude","CAP_EDGE",EDGE,{"disambiguationData":[OSD([sQuery(id+"F2.wireOp",EDGE,"E13.17.0")])],"isStart":true});
            var Q91;
            {var subQ0=sQuery(id+"F2.wireOp",EDGE,"E0");Q91=makeQuery(id+"F3.opExtrude","CAP_EDGE",EDGE,{"disambiguationData":[OSD([subQ0]),TDD([makeQuery(id+"F2.imprint","IMPRINT",EDGE,{"disambiguationData":[TD([[makeQuery(id+"F2.imprint","INTERSECT",VERTEX,{"derivedFrom":[subQ0,sQuery(id+"F2.wireOp",EDGE,"E13.16.2")]}),-1.0]])],"derivedFrom":subQ0})])],"isStart":true});}
            var Q92;
            Q92=makeQuery(id+"F3.opExtrude","CAP_EDGE",EDGE,{"disambiguationData":[OSD([sQuery(id+"F2.wireOp",EDGE,"E13.16.2")])],"isStart":true});
            var Q93;
            Q93=makeQuery(id+"F3.opExtrude","CAP_EDGE",EDGE,{"disambiguationData":[OSD([sQuery(id+"F2.wireOp",EDGE,"E13.16.0")])],"isStart":true});
            var Q94;
            {var subQ0=sQuery(id+"F2.wireOp",EDGE,"E0");Q94=makeQuery(id+"F3.opExtrude","CAP_EDGE",EDGE,{"disambiguationData":[OSD([subQ0]),TDD([makeQuery(id+"F2.imprint","IMPRINT",EDGE,{"disambiguationData":[TD([[makeQuery(id+"F2.imprint","INTERSECT",VERTEX,{"derivedFrom":[subQ0,sQuery(id+"F2.wireOp",EDGE,"E13.15.2")]}),-1.0]])],"derivedFrom":subQ0})])],"isStart":true});}
            var Q95;
            Q95=makeQuery(id+"F3.opExtrude","CAP_EDGE",EDGE,{"disambiguationData":[OSD([sQuery(id+"F2.wireOp",EDGE,"E13.15.2")])],"isStart":true});
            var Q96;
            Q96=makeQuery(id+"F3.opExtrude","CAP_EDGE",EDGE,{"disambiguationData":[OSD([sQuery(id+"F2.wireOp",EDGE,"E13.15.0")])],"isStart":true});
            var Q97;
            {var subQ0=sQuery(id+"F2.wireOp",EDGE,"E0");Q97=makeQuery(id+"F3.opExtrude","CAP_EDGE",EDGE,{"disambiguationData":[OSD([subQ0]),TDD([makeQuery(id+"F2.imprint","IMPRINT",EDGE,{"disambiguationData":[TD([[makeQuery(id+"F2.imprint","INTERSECT",VERTEX,{"derivedFrom":[subQ0,sQuery(id+"F2.wireOp",EDGE,"E13.14.2")]}),-1.0]])],"derivedFrom":subQ0})])],"isStart":true});}
            var Q98;
            Q98=makeQuery(id+"F3.opExtrude","CAP_EDGE",EDGE,{"disambiguationData":[OSD([sQuery(id+"F2.wireOp",EDGE,"E13.14.2")])],"isStart":true});
            var Q99;
            Q99=makeQuery(id+"F3.opExtrude","CAP_EDGE",EDGE,{"disambiguationData":[OSD([sQuery(id+"F2.wireOp",EDGE,"E13.14.0")])],"isStart":true});
            var Q100;
            {var subQ0=sQuery(id+"F2.wireOp",EDGE,"E0");Q100=makeQuery(id+"F3.opExtrude","CAP_EDGE",EDGE,{"disambiguationData":[OSD([subQ0]),TDD([makeQuery(id+"F2.imprint","IMPRINT",EDGE,{"disambiguationData":[TD([[makeQuery(id+"F2.imprint","INTERSECT",VERTEX,{"derivedFrom":[subQ0,sQuery(id+"F2.wireOp",EDGE,"E13.13.2")]}),-1.0]])],"derivedFrom":subQ0})])],"isStart":true});}
            var Q101;
            Q101=makeQuery(id+"F3.opExtrude","CAP_EDGE",EDGE,{"disambiguationData":[OSD([sQuery(id+"F2.wireOp",EDGE,"E13.13.2")])],"isStart":true});
            var Q102;
            Q102=makeQuery(id+"F3.opExtrude","CAP_EDGE",EDGE,{"disambiguationData":[OSD([sQuery(id+"F2.wireOp",EDGE,"E13.13.0")])],"isStart":true});
            var Q103;
            {var subQ0=sQuery(id+"F2.wireOp",EDGE,"E0");Q103=makeQuery(id+"F3.opExtrude","CAP_EDGE",EDGE,{"disambiguationData":[OSD([subQ0]),TDD([makeQuery(id+"F2.imprint","IMPRINT",EDGE,{"disambiguationData":[TD([[makeQuery(id+"F2.imprint","INTERSECT",VERTEX,{"derivedFrom":[subQ0,sQuery(id+"F2.wireOp",EDGE,"E13.12.2")]}),-1.0]])],"derivedFrom":subQ0})])],"isStart":true});}
            var Q104;
            Q104=makeQuery(id+"F3.opExtrude","CAP_EDGE",EDGE,{"disambiguationData":[OSD([sQuery(id+"F2.wireOp",EDGE,"E13.12.2")])],"isStart":true});
            var Q105;
            Q105=makeQuery(id+"F3.opExtrude","CAP_EDGE",EDGE,{"disambiguationData":[OSD([sQuery(id+"F2.wireOp",EDGE,"E13.12.0")])],"isStart":true});
            var Q106;
            {var subQ0=sQuery(id+"F2.wireOp",EDGE,"E0");Q106=makeQuery(id+"F3.opExtrude","CAP_EDGE",EDGE,{"disambiguationData":[OSD([subQ0]),TDD([makeQuery(id+"F2.imprint","IMPRINT",EDGE,{"disambiguationData":[TD([[makeQuery(id+"F2.imprint","INTERSECT",VERTEX,{"derivedFrom":[subQ0,sQuery(id+"F2.wireOp",EDGE,"E13.11.2")]}),-1.0]])],"derivedFrom":subQ0})])],"isStart":true});}
            var Q107;
            Q107=makeQuery(id+"F3.opExtrude","CAP_EDGE",EDGE,{"disambiguationData":[OSD([sQuery(id+"F2.wireOp",EDGE,"E13.11.2")])],"isStart":true});
            var Q108;
            Q108=makeQuery(id+"F3.opExtrude","CAP_EDGE",EDGE,{"disambiguationData":[OSD([sQuery(id+"F2.wireOp",EDGE,"E13.11.0")])],"isStart":true});
            var Q109;
            {var subQ0=sQuery(id+"F2.wireOp",EDGE,"E0");Q109=makeQuery(id+"F3.opExtrude","CAP_EDGE",EDGE,{"disambiguationData":[OSD([subQ0]),TDD([makeQuery(id+"F2.imprint","IMPRINT",EDGE,{"disambiguationData":[TD([[makeQuery(id+"F2.imprint","INTERSECT",VERTEX,{"derivedFrom":[subQ0,sQuery(id+"F2.wireOp",EDGE,"E13.10.2")]}),-1.0]])],"derivedFrom":subQ0})])],"isStart":true});}
            var Q110;
            Q110=makeQuery(id+"F3.opExtrude","CAP_EDGE",EDGE,{"disambiguationData":[OSD([sQuery(id+"F2.wireOp",EDGE,"E13.10.2")])],"isStart":true});
            var Q111;
            Q111=makeQuery(id+"F3.opExtrude","CAP_EDGE",EDGE,{"disambiguationData":[OSD([sQuery(id+"F2.wireOp",EDGE,"E13.10.0")])],"isStart":true});
            var Q112;
            {var subQ0=sQuery(id+"F2.wireOp",EDGE,"E0");Q112=makeQuery(id+"F3.opExtrude","CAP_EDGE",EDGE,{"disambiguationData":[OSD([subQ0]),TDD([makeQuery(id+"F2.imprint","IMPRINT",EDGE,{"disambiguationData":[TD([[makeQuery(id+"F2.imprint","INTERSECT",VERTEX,{"derivedFrom":[subQ0,sQuery(id+"F2.wireOp",EDGE,"E13.9.2")]}),-1.0]])],"derivedFrom":subQ0})])],"isStart":true});}
            var Q113;
            Q113=makeQuery(id+"F3.opExtrude","CAP_EDGE",EDGE,{"disambiguationData":[OSD([sQuery(id+"F2.wireOp",EDGE,"E13.9.2")])],"isStart":true});
            var Q114;
            Q114=makeQuery(id+"F3.opExtrude","CAP_EDGE",EDGE,{"disambiguationData":[OSD([sQuery(id+"F2.wireOp",EDGE,"E13.9.0")])],"isStart":true});
            var Q115;
            {var subQ0=sQuery(id+"F2.wireOp",EDGE,"E0");Q115=makeQuery(id+"F3.opExtrude","CAP_EDGE",EDGE,{"disambiguationData":[OSD([subQ0]),TDD([makeQuery(id+"F2.imprint","IMPRINT",EDGE,{"disambiguationData":[TD([[makeQuery(id+"F2.imprint","INTERSECT",VERTEX,{"derivedFrom":[subQ0,sQuery(id+"F2.wireOp",EDGE,"E13.8.2")]}),-1.0]])],"derivedFrom":subQ0})])],"isStart":true});}
            var Q116;
            Q116=makeQuery(id+"F3.opExtrude","CAP_EDGE",EDGE,{"disambiguationData":[OSD([sQuery(id+"F2.wireOp",EDGE,"E13.8.2")])],"isStart":true});
            fillet(context, id + "F4", {"entities" : qUnion([Q0, Q1, Q2, Q3, Q4, Q5, Q6, Q7, Q8, Q9, Q10, Q11, Q12, Q13, Q14, Q15, Q16, Q17, Q18, Q19, Q20, Q21, Q22, Q23, Q24, Q25, Q26, Q27, Q28, Q29, Q30, Q31, Q32, Q33, Q34, Q35, Q36, Q37, Q38, Q39, Q40, Q41, Q42, Q43, Q44, Q45, Q46, Q47, Q48, Q49, Q50, Q51, Q52, Q53, Q54, Q55, Q56, Q57, Q58, Q59, Q60, Q61, Q62, Q63, Q64, Q65, Q66, Q67, Q68, Q69, Q70, Q71, Q72, Q73, Q74, Q75, Q76, Q77, Q78, Q79, Q80, Q81, Q82, Q83, Q84, Q85, Q86, Q87, Q88, Q89, Q90, Q91, Q92, Q93, Q94, Q95, Q96, Q97, Q98, Q99, Q100, Q101, Q102, Q103, Q104, Q105, Q106, Q107, Q108, Q109, Q110, Q111, Q112, Q113, Q114, Q115, Q116]), "radius" : (getVariable(context, 'TeethFillet')) * mm, "tangentPropagation" : true, "allowEdgeOverflow" : false});
        }
    });
